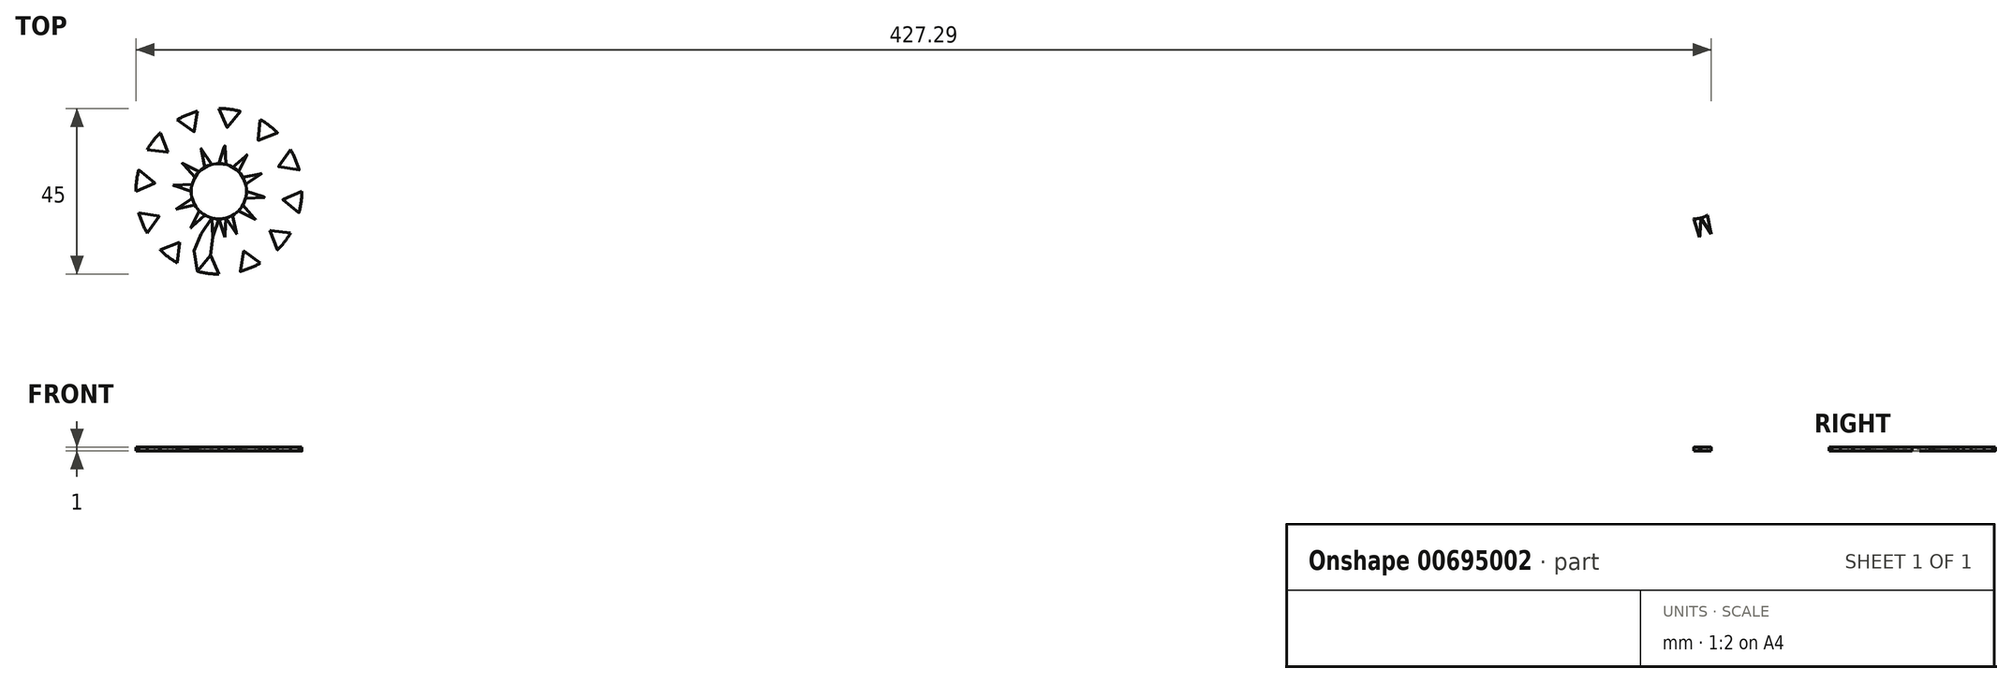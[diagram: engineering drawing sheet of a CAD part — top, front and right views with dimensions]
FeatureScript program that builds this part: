
annotation { "Feature Type Name" : "Feature", "Feature Type Description" : "" }
export const myFeature = defineFeature(function(context is Context, id is Id, definition is map)
    precondition{}
    {
        {
            var Q0;
            Q0=qCreatedBy(makeId("Top.planeOp"),FACE);
            var sketch = newSketch(context, id + "F0", { "sketchPlane" : qUnion([Q0])});
            skCircle(sketch, "E0", {"center": v(0, 0) * mm, "radius": 22.5 * mm, "construction": true});
            skLineSegment(sketch, "E1", {"start": v(0, 0) * mm, "end": v(0, -22.5) * mm, "construction": true});
            skLineSegment(sketch, "E2", {"start": v(0, 0) * mm, "end": v(-5.82, -21.73) * mm, "construction": true});
            skLineSegment(sketch, "E3", {"start": v(0, -22.5) * mm, "end": v(-5.82, -21.73) * mm, "construction": true});
            skLineSegment(sketch, "E4", {"start": v(-2.91, -22.12) * mm, "end": v(0, 0) * mm, "construction": true});
            skCircle(sketch, "E5", {"center": v(0, 0) * mm, "radius": 7.5 * mm, "construction": true});
            skCircle(sketch, "E6", {"center": v(0, 0) * mm, "radius": 12.5 * mm, "construction": true});
            skCircle(sketch, "E7", {"center": v(0, 0) * mm, "radius": 17.5 * mm, "construction": true});
            skLineSegment(sketch, "E8", {"start": v(0, -7.5) * mm, "end": v(-1.63, -12.4) * mm});
            skLineSegment(sketch, "E9", {"start": v(-1.63, -12.4) * mm, "end": v(-2.28, -17.35) * mm});
            skLineSegment(sketch, "E10", {"start": v(-2.28, -17.35) * mm, "end": v(0, -22.5) * mm});
            skArc(sketch, "E11", {"start": v(-5.82, -21.73) * mm, "mid": v(-2.94, -22.3) * mm, "end": v(0, -22.5) * mm});
            skArc(sketch, "E12", {"start": v(-1.94, -7.24) * mm, "mid": v(-0.98, -7.44) * mm, "end": v(0, -7.5) * mm});
            skLineSegment(sketch, "E13", {"start": v(0, 0) * mm, "end": v(-8.61, -20.79) * mm, "construction": true});
            skLineSegment(sketch, "E14", {"start": v(-1.94, -7.24) * mm, "end": v(-4.78, -11.55) * mm});
            skLineSegment(sketch, "E15", {"start": v(-4.78, -11.55) * mm, "end": v(-6.7, -16.17) * mm});
            skLineSegment(sketch, "E16", {"start": v(-6.7, -16.17) * mm, "end": v(-5.82, -21.73) * mm});
            skLineSegment(sketch, "E17", {"start": v(-1.94, -7.24) * mm, "end": v(-1.63, -12.4) * mm});
            skLineSegment(sketch, "E18", {"start": v(-5.82, -21.73) * mm, "end": v(-2.28, -17.35) * mm});
            skSolve(sketch);
        }
        {
            var Q0;
            Q0=makeQuery(id+"F0.imprint","IMPRINT",FACE,{"disambiguationData":[TD([[makeQuery(id+"F0.imprint","IMPRINT",EDGE,{"derivedFrom":sQuery(id+"F0.wireOp",EDGE,"E8")}),-1.0]])]});
            var Q1;
            Q1=makeQuery(id+"F0.imprint","IMPRINT",FACE,{"disambiguationData":[TD([[makeQuery(id+"F0.imprint","IMPRINT",EDGE,{"derivedFrom":sQuery(id+"F0.wireOp",EDGE,"E10")}),-1.0]])]});
            extrude(context, id + "F1", {"entities" : qUnion([Q0, Q1]), "oppositeDirection" : true, "depth" : 1 * mm, "offsetDistance" : 25 * mm});
        }
        {
            var Q0;
            Q0=makeQuery(id+"F0.imprint","IMPRINT",FACE,{"disambiguationData":[TD([[makeQuery(id+"F0.imprint","IMPRINT",EDGE,{"derivedFrom":sQuery(id+"F0.wireOp",EDGE,"E9")}),-1.0]])]});
            extrude(context, id + "F2", {"entities" : qUnion([Q0]), "oppositeDirection" : true, "depth" : 1 * mm, "offsetDistance" : 25 * mm});
        }
        {
            var Q0;
            Q0=makeQuery(id+"F1.opExtrude","CAP_EDGE",EDGE,{"disambiguationData":[OSD([sQuery(id+"F0.wireOp",EDGE,"E17")])],"isStart":true});
            var Q1;
            Q1=makeQuery(id+"F1.opExtrude","CAP_EDGE",EDGE,{"disambiguationData":[OSD([sQuery(id+"F0.wireOp",EDGE,"E18")])],"isStart":true});
            var Q2;
            Q2=makeQuery(id+"F2.opExtrude","CAP_EDGE",EDGE,{"disambiguationData":[OSD([sQuery(id+"F0.wireOp",EDGE,"E18")])],"isStart":true});
            var Q3;
            Q3=makeQuery(id+"F2.opExtrude","CAP_EDGE",EDGE,{"disambiguationData":[OSD([sQuery(id+"F0.wireOp",EDGE,"E17")])],"isStart":true});
            var Q4;
            Q4=makeQuery(id+"F2.opExtrude","CAP_FACE",FACE,{"disambiguationData":[OSD([sQuery(id+"F0.wireOp",EDGE,"E9"),sQuery(id+"F0.wireOp",EDGE,"E14"),sQuery(id+"F0.wireOp",EDGE,"E15"),sQuery(id+"F0.wireOp",EDGE,"E16"),sQuery(id+"F0.wireOp",EDGE,"E17"),sQuery(id+"F0.wireOp",EDGE,"E18")])],"isStart":true});
            fillet(context, id + "F3", {"entities" : qUnion([Q0, Q1, Q2, Q3, Q4]), "radius" : 0.2 * mm, "tangentPropagation" : true, "allowEdgeOverflow" : false});
        }
        {
            var Q0;
            Q0=qCreatedBy(makeId("Right.planeOp"),FACE);
            var sketch = newSketch(context, id + "F4", { "sketchPlane" : qUnion([Q0])});
            skLineSegment(sketch, "E19", {"start": v(0, 0) * mm, "end": v(-22.5, 0) * mm, "construction": true});
            skLineSegment(sketch, "E20", {"start": v(0, 0) * mm, "end": v(0, -120) * mm, "construction": true});
            skLineSegment(sketch, "E21", {"start": v(-22.5, 0) * mm, "end": v(-22.5, -119.3) * mm, "construction": true});
            skLineSegment(sketch, "E22", {"start": v(-27.61, -5) * mm, "end": v(-27.61, -15) * mm});
            skFitSpline(sketch, "E23", {"points": [v(0, -120) * mm, v(-27.61, -122.1) * mm], "startDerivative": vector(-25.7, 0.17) * mm, "endDerivative": vector(-15.34, -4.86) * mm});
            skArc(sketch, "E24.filletArc", {"start": v(-27.61, -118.37) * mm, "mid": v(-26.56, -120.65) * mm, "end": v(-24.14, -121.33) * mm});
            skLineSegment(sketch, "E25", {"start": v(-22.5, 0) * mm, "end": v(-22.61, 0) * mm});
            skPoint(sketch, "E26.visualSharp", {"position": v(-27.61, 0) * mm});
            skArc(sketch, "E26.filletArc", {"start": v(-22.61, 0) * mm, "mid": v(-26.15, -1.46) * mm, "end": v(-27.61, -5) * mm});
            skLineSegment(sketch, "E27.trimOffspring", {"start": v(-27.61, -16) * mm, "end": v(-27.61, -118.37) * mm});
            skLineSegment(sketch, "E28.0", {"start": v(-26.61, -5) * mm, "end": v(-26.61, -15) * mm});
            skArc(sketch, "E28.1", {"start": v(-22.61, -1) * mm, "mid": v(-25.44, -2.17) * mm, "end": v(-26.61, -5) * mm});
            skLineSegment(sketch, "E29", {"start": v(-22.5, 0) * mm, "end": v(-22.61, -1) * mm});
            skLineSegment(sketch, "E30", {"start": v(-26.61, -15) * mm, "end": v(-27.61, -15) * mm});
            skFitSpline(sketch, "E31.0", {"points": [v(0, -119) * mm, v(-2.15, -118.99) * mm, v(-7.12, -119.03) * mm, v(-13.91, -119.31) * mm, v(-19.03, -119.7) * mm, v(-22.55, -120.07) * mm, v(-25.6, -120.54) * mm, v(-27.22, -120.92) * mm, v(-27.92, -121.14) * mm]});
            skLineSegment(sketch, "E31.1", {"start": v(-26.61, -16) * mm, "end": v(-26.61, -118.37) * mm});
            skLineSegment(sketch, "E32", {"start": v(-26.61, -16) * mm, "end": v(-27.61, -16) * mm});
            skLineSegment(sketch, "E33", {"start": v(0, -119) * mm, "end": v(0, -120) * mm});
            skPoint(sketch, "E34.visualSharp", {"position": v(-26.61, -120.79) * mm});
            skArc(sketch, "E34.filletArc", {"start": v(-26.61, -118.37) * mm, "mid": v(-25.91, -119.9) * mm, "end": v(-24.3, -120.34) * mm});
            skSolve(sketch);
        }
        {
            var Q0;
            Q0 = qSketchRegion(id + "F4", true);
            var Q1;
            Q1=sQuery(id+"F4.wireOp",EDGE,"E22");
            var Q2;
            Q2=sQuery(id+"F4.wireOp",EDGE,"E26.filletArc");
            var Q3;
            Q3=sQuery(id+"F4.wireOp",EDGE,"E24.filletArc");
            var Q4;
            Q4=sQuery(id+"F4.wireOp",EDGE,"E23");
            var Q5;
            Q5=sQuery(id+"F4.wireOp",EDGE,"E27.trimOffspring");
            var Q6;
            Q6=sQuery(id+"F4.wireOp",EDGE,"E20");
            revolve(context, id + "F5", {"bodyType" : ToolBodyType.SURFACE, "entities" : qUnion([Q0]), "surfaceEntities" : qUnion([Q1, Q2, Q3, Q4, Q5]), "axis" : qUnion([Q6]), "revolveType" : RevolveType.FULL});
        }
        {
            var Q0;
            Q0=makeQuery(id+"F1.opExtrude","SWEPT_BODY",BODY,{"disambiguationData":[OSD([sQuery(id+"F0.wireOp",EDGE,"E8"),sQuery(id+"F0.wireOp",EDGE,"E9"),sQuery(id+"F0.wireOp",EDGE,"E10"),sQuery(id+"F0.wireOp",EDGE,"E11"),sQuery(id+"F0.wireOp",EDGE,"E12"),sQuery(id+"F0.wireOp",EDGE,"E14"),sQuery(id+"F0.wireOp",EDGE,"E15"),sQuery(id+"F0.wireOp",EDGE,"E16")])]});
            var Q1;
            Q1=sQuery(id+"F4.wireOp",EDGE,"E20");
            circularPattern(context, id + "F6", {"entities" : qUnion([Q0]), "axis" : qUnion([Q1]), "angle" : 360 * degree, "instanceCount" : 12, "equalSpace" : true});
        }
        {
            var Q0;
            Q0=qCreatedBy(makeId("Top.planeOp"),FACE);
            var sketch = newSketch(context, id + "F7", { "sketchPlane" : qUnion([Q0])});
            skCircle(sketch, "E35", {"center": v(0, 0) * mm, "radius": 7.5 * mm});
            skSolve(sketch);
        }
        {
            var Q0;
            Q0=makeQuery(id+"F7.imprint","IMPRINT",FACE,{"disambiguationData":[TD([[makeQuery(id+"F7.imprint","IMPRINT",EDGE,{"derivedFrom":sQuery(id+"F7.wireOp",EDGE,"E35")}),1.0]])]});
            var Q1;
            Q1=sQuery(id+"F7.wireOp",EDGE,"E35");
            extrude(context, id + "F8", {"entities" : qUnion([Q0]), "surfaceEntities" : qUnion([Q1]), "oppositeDirection" : true, "depth" : 1 * mm, "offsetDistance" : 25 * mm});
        }
        {
            var Q0;
            Q0=makeQuery(id+"F6.opPattern","COPY",BODY,{"derivedFrom":makeQuery(id+"F1.opExtrude","SWEPT_BODY",BODY,{"disambiguationData":[OSD([sQuery(id+"F0.wireOp",EDGE,"E8"),sQuery(id+"F0.wireOp",EDGE,"E12"),sQuery(id+"F0.wireOp",EDGE,"E17")])]}),"instanceName":"11"});
            var Q1;
            Q1=sQuery(id+"F4.wireOp",EDGE,"E20");
            circularPattern(context, id + "F9", {"entities" : qUnion([Q0]), "axis" : qUnion([Q1]), "angle" : 15 * degree, "instanceCount" : 2});
        }
        {
            var Q0;
            Q0=makeQuery(id+"F6.opPattern","COPY",BODY,{"derivedFrom":makeQuery(id+"F1.opExtrude","SWEPT_BODY",BODY,{"disambiguationData":[OSD([sQuery(id+"F0.wireOp",EDGE,"E8"),sQuery(id+"F0.wireOp",EDGE,"E12"),sQuery(id+"F0.wireOp",EDGE,"E17")])]}),"instanceName":"11"});
            var Q1;
            Q1=makeQuery(id+"F5.opRevolve","SWEPT_BODY",BODY,{"disambiguationData":[OSD([sQuery(id+"F4.wireOp",EDGE,"E26.filletArc")])]});
            var Q2;
            Q2=makeQuery(id+"F5.opRevolve","SWEPT_BODY",BODY,{"disambiguationData":[OSD([sQuery(id+"F4.wireOp",EDGE,"E27.trimOffspring")])]});
            var Q3;
            Q3=makeQuery(id+"F9.opPattern","COPY",BODY,{"derivedFrom":makeQuery(id+"F6.opPattern","COPY",BODY,{"derivedFrom":makeQuery(id+"F1.opExtrude","SWEPT_BODY",BODY,{"disambiguationData":[OSD([sQuery(id+"F0.wireOp",EDGE,"E8"),sQuery(id+"F0.wireOp",EDGE,"E12"),sQuery(id+"F0.wireOp",EDGE,"E17")])]}),"instanceName":"11"}),"instanceName":"1"});
            transform(context, id + "F10", {"entities" : qUnion([Q0, Q1, Q2, Q3]), "transformType" : TransformType.TRANSLATION_3D, "dx" : 400 * mm, "dy" : 0 * mm, "dz" : 0 * mm, "makeCopy" : true});
        }
    });
